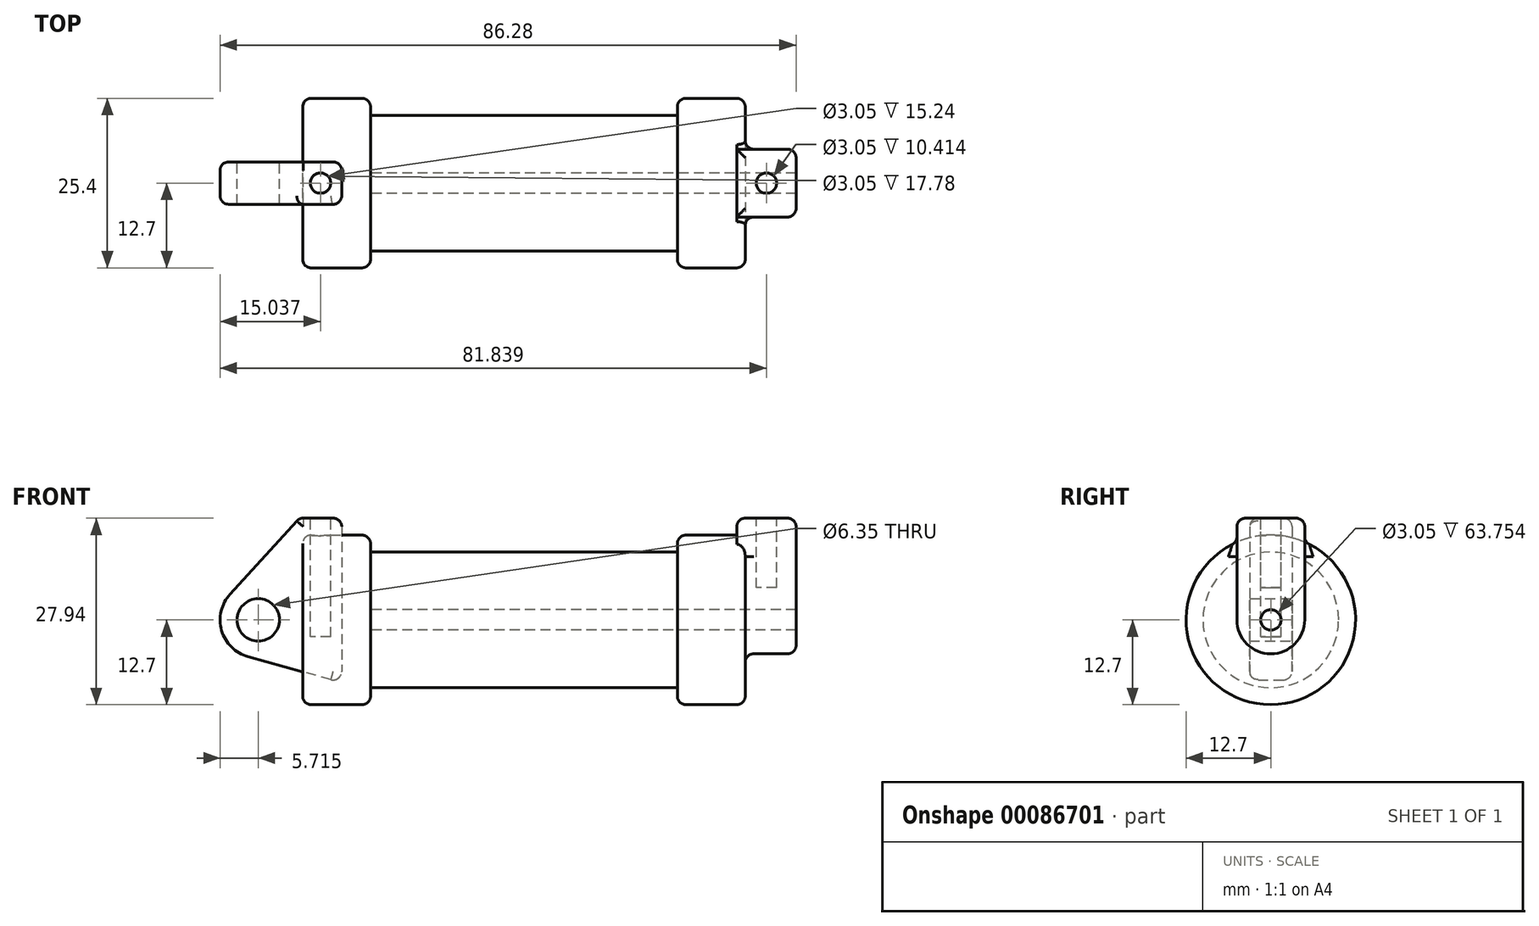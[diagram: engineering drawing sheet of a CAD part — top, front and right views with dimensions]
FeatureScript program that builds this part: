
annotation { "Feature Type Name" : "Feature", "Feature Type Description" : "" }
export const myFeature = defineFeature(function(context is Context, id is Id, definition is map)
    precondition{}
    {
        {
            var Q0;
            Q0=qCreatedBy(makeId("Front.planeOp"),FACE);
            var sketch = newSketch(context, id + "F0", { "sketchPlane" : qUnion([Q0])});
            skLineSegment(sketch, "E0", {"start": v(0, 0) * mm, "end": v(0, 12.7) * mm});
            skLineSegment(sketch, "E1", {"start": v(0, 12.7) * mm, "end": v(10.16, 12.7) * mm});
            skLineSegment(sketch, "E2", {"start": v(10.16, 12.7) * mm, "end": v(10.16, 10.16) * mm});
            skLineSegment(sketch, "E3", {"start": v(10.16, 10.16) * mm, "end": v(56.13, 10.16) * mm});
            skLineSegment(sketch, "E4", {"start": v(56.13, 10.16) * mm, "end": v(56.13, 12.7) * mm});
            skLineSegment(sketch, "E5", {"start": v(56.13, 12.7) * mm, "end": v(66.3, 12.7) * mm});
            skLineSegment(sketch, "E6", {"start": v(66.3, 12.7) * mm, "end": v(66.3, 0) * mm});
            skLineSegment(sketch, "E7", {"start": v(66.3, 0) * mm, "end": v(0, 0) * mm});
            skLineSegment(sketch, "E8", {"start": v(5.84, 15.24) * mm, "end": v(-0.5, 15.24) * mm});
            skLineSegment(sketch, "E9", {"start": v(-0.5, 15.24) * mm, "end": v(-10.88, 3.85) * mm});
            skLineSegment(sketch, "E10", {"start": v(0, 0) * mm, "end": v(-6.65, 0) * mm});
            skCircle(sketch, "E11", {"center": v(-6.65, 0) * mm, "radius": 5.72 * mm});
            skCircle(sketch, "E12", {"center": v(-6.65, 0) * mm, "radius": 3.18 * mm});
            skLineSegment(sketch, "E13", {"start": v(5.84, 15.24) * mm, "end": v(5.84, -9.4) * mm});
            skLineSegment(sketch, "E14", {"start": v(5.84, -9.4) * mm, "end": v(-8.18, -5.5) * mm});
            skSolve(sketch);
        }
        {
            var Q0;
            {var subQ3=sQuery(id+"F0.wireOp",EDGE,"E0");Q0=makeQuery(id+"F0.imprint","IMPRINT",FACE,{"disambiguationData":[TD([[makeQuery(id+"F0.imprint","IMPRINT",EDGE,{"derivedFrom":subQ3}),1.0]])]});}
            var Q1;
            {var subQ0=sQuery(id+"F0.wireOp",EDGE,"E14");Q1=makeQuery(id+"F0.imprint","IMPRINT",FACE,{"disambiguationData":[TD([[makeQuery(id+"F0.imprint","IMPRINT",EDGE,{"derivedFrom":subQ0}),-1.0]])]});}
            var Q2;
            {var subQ0=sQuery(id+"F0.wireOp",EDGE,"E0");Q2=makeQuery(id+"F0.imprint","IMPRINT",FACE,{"disambiguationData":[TD([[makeQuery(id+"F0.imprint","IMPRINT",EDGE,{"derivedFrom":subQ0}),-1.0]])]});}
            var Q3;
            {var subQ4=sQuery(id+"F0.wireOp",EDGE,"E12");Q3=makeQuery(id+"F0.imprint","IMPRINT",FACE,{"disambiguationData":[TD([[makeQuery(id+"F0.imprint","IMPRINT",EDGE,{"derivedFrom":subQ4}),-1.0]])]});}
            extrude(context, id + "F1", {"entities" : qUnion([Q0, Q1, Q2, Q3]), "endBound" : BoundingType.SYMMETRIC, "depth" : 6.35 * mm});
        }
        {
            var Q0;
            {var subQ0=sQuery(id+"F0.wireOp",EDGE,"E2");Q0=makeQuery(id+"F0.imprint","IMPRINT",FACE,{"disambiguationData":[TD([[makeQuery(id+"F0.imprint","IMPRINT",EDGE,{"derivedFrom":subQ0}),-1.0]])]});}
            var Q1;
            {var subQ0=sQuery(id+"F0.wireOp",EDGE,"E0");Q1=makeQuery(id+"F0.imprint","IMPRINT",FACE,{"disambiguationData":[TD([[makeQuery(id+"F0.imprint","IMPRINT",EDGE,{"derivedFrom":subQ0}),-1.0]])]});}
            var Q2;
            Q2=sQuery(id+"F0.wireOp",EDGE,"E7");
            revolve(context, id + "F2", {"entities" : qUnion([Q0, Q1]), "axis" : qUnion([Q2]), "revolveType" : RevolveType.FULL});
        }
        {
            var Q0;
            Q0=makeQuery(id+"F2.opRevolve","SWEPT_FACE",FACE,{"disambiguationData":[OSD([sQuery(id+"F0.wireOp",EDGE,"E6")])]});
            var sketch = newSketch(context, id + "F3", { "sketchPlane" : qUnion([Q0])});
            skCircle(sketch, "E15", {"center": v(0, 0) * mm, "radius": 1.52 * mm});
            skCircle(sketch, "E16", {"center": v(0, 0) * mm, "radius": 5.08 * mm});
            skLineSegment(sketch, "E17", {"start": v(5.08, 0) * mm, "end": v(5.08, 15.24) * mm});
            skLineSegment(sketch, "E18", {"start": v(-5.08, 0) * mm, "end": v(-5.08, 15.24) * mm});
            skLineSegment(sketch, "E19", {"start": v(-5.08, 15.24) * mm, "end": v(5.08, 15.24) * mm});
            skSolve(sketch);
        }
        {
            var Q0;
            {var subQ0=sQuery(id+"F3.wireOp",EDGE,"E19");Q0=makeQuery(id+"F3.imprint","IMPRINT",FACE,{"disambiguationData":[TD([[makeQuery(id+"F3.imprint","IMPRINT",EDGE,{"derivedFrom":subQ0}),-1.0]])]});}
            var Q1;
            {var subQ0=sQuery(id+"F3.wireOp",EDGE,"E17");var subQ1=sQuery(id+"F3.wireOp",EDGE,"E16");var subQ2=makeQuery(id+"F3.imprint","INTERSECT",VERTEX,{"derivedFrom":[subQ1,subQ0]});Q1=makeQuery(id+"F3.imprint","IMPRINT",FACE,{"disambiguationData":[TD([[makeQuery(id+"F3.imprint","IMPRINT",EDGE,{"disambiguationData":[TD([[subQ2,-1.0]])],"derivedFrom":subQ1}),-1.0]])]});}
            var Q2;
            Q2=makeQuery(id+"F3.imprint","IMPRINT",FACE,{"disambiguationData":[TD([[makeQuery(id+"F3.imprint","IMPRINT",EDGE,{"derivedFrom":sQuery(id+"F3.wireOp",EDGE,"E15")}),-1.0]])]});
            extrude(context, id + "F4", {"entities" : qUnion([Q0, Q1, Q2]), "operationType" : NewBodyOperationType.ADD, "depth" : 7.62 * mm, "hasSecondDirection" : true, "secondDirectionOppositeDirection" : true, "secondDirectionDepth" : 1.27 * mm});
        }
        {
            var Q0;
            Q0=makeQuery(id+"F4.boolean.opBoolean","SPLIT",FACE,{"disambiguationData":[TD([makeQuery(id+"F4.opExtrude","SWEPT_FACE",FACE,{"disambiguationData":[OSD([sQuery(id+"F3.wireOp",EDGE,"E15")])]})])],"derivedFrom":makeQuery(id+"F2.opRevolve","SWEPT_FACE",FACE,{"disambiguationData":[OSD([sQuery(id+"F0.wireOp",EDGE,"E6")])]})});
            var Q1;
            Q1=makeQuery(id+"F2.opRevolve","SWEPT_FACE",FACE,{"disambiguationData":[OSD([sQuery(id+"F0.wireOp",EDGE,"E2")])]});
            extrude(context, id + "F5", {"entities" : qUnion([Q0]), "operationType" : NewBodyOperationType.REMOVE, "endBound" : BoundingType.UP_TO_SURFACE, "oppositeDirection" : true, "endBoundEntityFace" : qUnion([Q1]), "depth" : 25.4 * mm});
        }
        {
            var Q0;
            Q0=makeQuery(id+"F1.opExtrude","SWEPT_FACE",FACE,{"disambiguationData":[OSD([sQuery(id+"F0.wireOp",EDGE,"E8")])]});
            var sketch = newSketch(context, id + "F6", { "sketchPlane" : qUnion([Q0])});
            skLineSegment(sketch, "E20", {"start": v(2.67, 3.18) * mm, "end": v(2.67, -3.18) * mm, "construction": true});
            skCircle(sketch, "E21", {"center": v(2.67, 0) * mm, "radius": 1.52 * mm});
            skSolve(sketch);
        }
        {
            var Q0;
            Q0=makeQuery(id+"F6.imprint","IMPRINT",FACE,{"disambiguationData":[TD([[makeQuery(id+"F6.imprint","IMPRINT",EDGE,{"derivedFrom":sQuery(id+"F6.wireOp",EDGE,"E21")}),1.0]])]});
            var Q1;
            Q1=sQuery(id+"F6.wireOp",EDGE,"E21");
            extrude(context, id + "F7", {"entities" : qUnion([Q0]), "operationType" : NewBodyOperationType.REMOVE, "surfaceEntities" : qUnion([Q1]), "oppositeDirection" : true, "depth" : 17.78 * mm});
        }
        {
            var Q0;
            Q0=makeQuery(id+"F4.opExtrude","SWEPT_FACE",FACE,{"disambiguationData":[OSD([sQuery(id+"F3.wireOp",EDGE,"E19")])]});
            var sketch = newSketch(context, id + "F8", { "sketchPlane" : qUnion([Q0])});
            skLineSegment(sketch, "E22", {"start": v(69.47, 5.08) * mm, "end": v(69.47, -5.08) * mm, "construction": true});
            skCircle(sketch, "E23", {"center": v(69.47, 0) * mm, "radius": 1.52 * mm});
            skSolve(sketch);
        }
        {
            var Q0;
            Q0=makeQuery(id+"F8.imprint","IMPRINT",FACE,{"disambiguationData":[TD([[makeQuery(id+"F8.imprint","IMPRINT",EDGE,{"derivedFrom":sQuery(id+"F8.wireOp",EDGE,"E23")}),1.0]])]});
            extrude(context, id + "F9", {"entities" : qUnion([Q0]), "operationType" : NewBodyOperationType.REMOVE, "oppositeDirection" : true, "depth" : 10.4 * mm});
        }
        {
            var Q0;
            Q0=makeQuery(id+"F2.opRevolve","SWEPT_EDGE",EDGE,{"disambiguationData":[OSD([sQuery(id+"F0.wireOp",EDGE,"E1"),sQuery(id+"F0.wireOp",EDGE,"E2")])]});
            var Q1;
            Q1=makeQuery(id+"F2.opRevolve","SWEPT_EDGE",EDGE,{"disambiguationData":[OSD([sQuery(id+"F0.wireOp",EDGE,"E0"),sQuery(id+"F0.wireOp",EDGE,"E1")])]});
            var Q2;
            Q2=makeQuery(id+"F2.opRevolve","SWEPT_EDGE",EDGE,{"disambiguationData":[OSD([sQuery(id+"F0.wireOp",EDGE,"E4"),sQuery(id+"F0.wireOp",EDGE,"E5")])]});
            var Q3;
            Q3=makeQuery(id+"F2.opRevolve","SWEPT_EDGE",EDGE,{"disambiguationData":[OSD([sQuery(id+"F0.wireOp",EDGE,"E5"),sQuery(id+"F0.wireOp",EDGE,"E6")])]});
            fillet(context, id + "F10", {"entities" : qUnion([Q0, Q1, Q2, Q3]), "radius" : 1.27 * mm, "tangentPropagation" : true, "allowEdgeOverflow" : false});
        }
        {
            var Q0;
            Q0=makeQuery(id+"F4.opExtrude","SWEPT_EDGE",EDGE,{"disambiguationData":[OSD([sQuery(id+"F3.wireOp",EDGE,"E17"),sQuery(id+"F3.wireOp",EDGE,"E19")])]});
            var Q1;
            Q1=makeQuery(id+"F4.opExtrude","CAP_EDGE",EDGE,{"disambiguationData":[OSD([sQuery(id+"F3.wireOp",EDGE,"E19")])],"isStart":false});
            var Q2;
            Q2=makeQuery(id+"F4.opExtrude","SWEPT_EDGE",EDGE,{"disambiguationData":[OSD([sQuery(id+"F3.wireOp",EDGE,"E18"),sQuery(id+"F3.wireOp",EDGE,"E19")])]});
            var Q3;
            Q3=makeQuery(id+"F4.opExtrude","CAP_EDGE",EDGE,{"disambiguationData":[OSD([sQuery(id+"F3.wireOp",EDGE,"E19")])],"isStart":true});
            fillet(context, id + "F11", {"entities" : qUnion([Q0, Q1, Q2, Q3]), "radius" : 1.27 * mm, "tangentPropagation" : true, "allowEdgeOverflow" : false});
        }
        {
            var Q0;
            Q0=makeQuery(id+"F4.opExtrude","CAP_EDGE",EDGE,{"disambiguationData":[OSD([sQuery(id+"F3.wireOp",EDGE,"E18")])],"isStart":false});
            var Q1;
            Q1=makeQuery(id+"F4.opExtrude","CAP_EDGE",EDGE,{"disambiguationData":[OSD([sQuery(id+"F3.wireOp",EDGE,"E16")])],"isStart":false});
            var Q2;
            Q2=makeQuery(id+"F4.opExtrude","CAP_EDGE",EDGE,{"disambiguationData":[OSD([sQuery(id+"F3.wireOp",EDGE,"E17")])],"isStart":false});
            var Q3;
            Q3=makeQuery(id+"F10.opFillet","BLEND_EDGE",EDGE,{"blendedFrom":[makeQuery(id+"F2.opRevolve","SWEPT_EDGE",EDGE,{"disambiguationData":[OSD([sQuery(id+"F0.wireOp",EDGE,"E5"),sQuery(id+"F0.wireOp",EDGE,"E6")])]}),makeQuery(id+"F4.opExtrude","SWEPT_FACE",FACE,{"disambiguationData":[OSD([sQuery(id+"F3.wireOp",EDGE,"E18")])]})],"blendedInto":[makeQuery(id+"F4.opExtrude","SWEPT_FACE",FACE,{"disambiguationData":[OSD([sQuery(id+"F3.wireOp",EDGE,"E18")])]})]});
            var Q4;
            Q4=makeQuery(id+"F4.boolean.opBoolean","INTERSECT",EDGE,{"derivedFrom":[makeQuery(id+"F2.opRevolve","SWEPT_FACE",FACE,{"disambiguationData":[OSD([sQuery(id+"F0.wireOp",EDGE,"E6")])]}),makeQuery(id+"F4.opExtrude","SWEPT_FACE",FACE,{"disambiguationData":[OSD([sQuery(id+"F3.wireOp",EDGE,"E18")])]})]});
            fillet(context, id + "F12", {"entities" : qUnion([Q0, Q1, Q2, Q3, Q4]), "radius" : 1.27 * mm, "tangentPropagation" : true, "allowEdgeOverflow" : false});
        }
        {
            var Q0;
            Q0=makeQuery(id+"F1.opExtrude","SWEPT_EDGE",EDGE,{"disambiguationData":[OSD([sQuery(id+"F0.wireOp",EDGE,"E8"),sQuery(id+"F0.wireOp",EDGE,"E13")])]});
            fillet(context, id + "F13", {"entities" : qUnion([Q0]), "radius" : 1.27 * mm, "tangentPropagation" : true, "allowEdgeOverflow" : false});
        }
        {
            var Q0;
            Q0=makeQuery(id+"F1.opExtrude","CAP_EDGE",EDGE,{"disambiguationData":[OSD([sQuery(id+"F0.wireOp",EDGE,"E8")])],"isStart":false});
            var Q1;
            Q1=makeQuery(id+"F1.opExtrude","CAP_EDGE",EDGE,{"disambiguationData":[OSD([sQuery(id+"F0.wireOp",EDGE,"E11")])],"isStart":false});
            fillet(context, id + "F14", {"entities" : qUnion([Q0, Q1]), "radius" : 1.27 * mm, "tangentPropagation" : true, "allowEdgeOverflow" : false});
        }
        {
            var Q0;
            Q0=makeQuery(id+"F1.opExtrude","CAP_EDGE",EDGE,{"disambiguationData":[OSD([sQuery(id+"F0.wireOp",EDGE,"E8")])],"isStart":true});
            fillet(context, id + "F15", {"entities" : qUnion([Q0]), "radius" : 1.27 * mm, "tangentPropagation" : true, "allowEdgeOverflow" : false});
        }
        {
            var Q0;
            Q0=makeQuery(id+"F1.opExtrude","SWEPT_EDGE",EDGE,{"disambiguationData":[OSD([sQuery(id+"F0.wireOp",EDGE,"E8"),sQuery(id+"F0.wireOp",EDGE,"E9")])]});
            fillet(context, id + "F16", {"entities" : qUnion([Q0]), "radius" : 1.27 * mm, "tangentPropagation" : true, "allowEdgeOverflow" : false});
        }
    });
